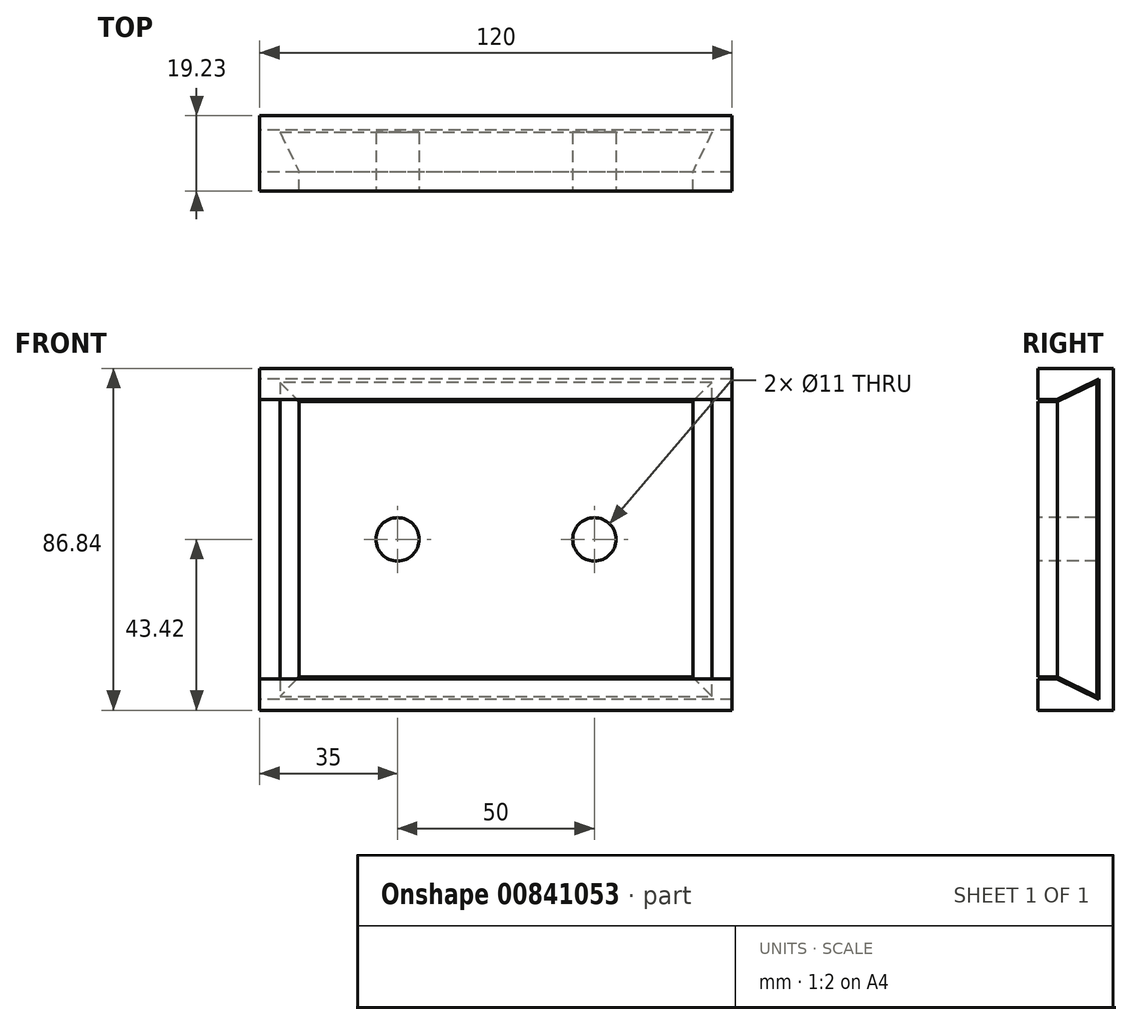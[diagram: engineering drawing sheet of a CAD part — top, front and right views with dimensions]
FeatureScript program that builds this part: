
annotation { "Feature Type Name" : "Feature", "Feature Type Description" : "" }
export const myFeature = defineFeature(function(context is Context, id is Id, definition is map)
    precondition{}
    {
        {
            var Q0;
            Q0=qCreatedBy(makeId("Front.planeOp"),FACE);
            var sketch = newSketch(context, id + "F0", { "sketchPlane" : qUnion([Q0])});
            skLineSegment(sketch, "E0.bottom", {"start": v(-50, -35) * mm, "end": v(50, -35) * mm});
            skLineSegment(sketch, "E0.top", {"start": v(-50, 35) * mm, "end": v(50, 35) * mm});
            skLineSegment(sketch, "E0.left", {"start": v(-50, -35) * mm, "end": v(-50, 35) * mm});
            skLineSegment(sketch, "E0.right", {"start": v(50, -35) * mm, "end": v(50, 35) * mm});
            skSolve(sketch);
        }
        {
            var Q0;
            Q0=makeQuery(id+"F0.imprint","IMPRINT",FACE,{"disambiguationData":[TD([[makeQuery(id+"F0.imprint","IMPRINT",EDGE,{"derivedFrom":sQuery(id+"F0.wireOp",EDGE,"E0.bottom")}),1.0]])]});
            extrude(context, id + "F1", {"entities" : qUnion([Q0]), "oppositeDirection" : true, "depth" : 10 * mm, "offsetDistance" : 25 * mm, "hasDraft" : true, "draftAngle" : 26 * degree});
        }
        {
            var Q0;
            Q0=makeQuery(id+"F1.opExtrude","CAP_FACE",FACE,{"disambiguationData":[OSD([sQuery(id+"F0.wireOp",EDGE,"E0.bottom"),sQuery(id+"F0.wireOp",EDGE,"E0.top"),sQuery(id+"F0.wireOp",EDGE,"E0.left"),sQuery(id+"F0.wireOp",EDGE,"E0.right")])],"isStart":true});
            extrude(context, id + "F2", {"entities" : qUnion([Q0]), "operationType" : NewBodyOperationType.ADD, "depth" : 5 * mm, "offsetDistance" : 25 * mm});
        }
        {
            var Q0;
            Q0=makeQuery(id+"F2.opExtrude","CAP_FACE",FACE,{"disambiguationData":[OSD([sQuery(id+"F0.wireOp",EDGE,"E0.bottom"),sQuery(id+"F0.wireOp",EDGE,"E0.top"),sQuery(id+"F0.wireOp",EDGE,"E0.left"),sQuery(id+"F0.wireOp",EDGE,"E0.right")])],"isStart":false});
            var sketch = newSketch(context, id + "F3", { "sketchPlane" : qUnion([Q0])});
            skPoint(sketch, "E1", {"position": v(-25, 0) * mm});
            skPoint(sketch, "E2", {"position": v(25, 0) * mm});
            skSolve(sketch);
        }
        {
            var Q0;
            Q0=sQuery(id+"F3.wireOp",VERTEX,"E1");
            var Q1;
            Q1=sQuery(id+"F3.wireOp",VERTEX,"E2");
            var Q2;
            Q2=makeQuery(id+"F1.opExtrude","SWEPT_BODY",BODY,{"disambiguationData":[OSD([sQuery(id+"F0.wireOp",EDGE,"E0.bottom"),sQuery(id+"F0.wireOp",EDGE,"E0.top"),sQuery(id+"F0.wireOp",EDGE,"E0.left"),sQuery(id+"F0.wireOp",EDGE,"E0.right")])]});
            hole(context, id + "F4", {"style" : HoleStyle.SIMPLE, "endStyle" : HoleEndStyle.THROUGH, "standardTappedOrClearance" : lookupTablePath({ "fit" : "Normal", "standard" : "ISO", "size" : "M10", "type" : "Clearance" }), "standardBlindInLast" : lookupTablePath({ "fit" : "Standard", "standard" : "ISO", "size" : "M10", "type" : "Clearance" }), "holeDiameter" : 11 * mm, "majorDiameter" : 5 * mm, "isTappedThrough" : true, "tappedDepth" : 12 * mm, "tapClearance" : 3, "locations" : qUnion([Q0, Q1]), "scope" : qUnion([Q2])});
        }
        {
            var Q0;
            Q0=qCreatedBy(makeId("Right.planeOp"),FACE);
            var sketch = newSketch(context, id + "F5", { "sketchPlane" : qUnion([Q0])});
            skLineSegment(sketch, "E3.0", {"start": v(-5, 35.5) * mm, "end": v(-0.12, 35.5) * mm});
            skLineSegment(sketch, "E3.1", {"start": v(-5, -35.5) * mm, "end": v(-0.12, -35.5) * mm});
            skLineSegment(sketch, "E3.2", {"start": v(10.5, -40.68) * mm, "end": v(-0.12, -35.5) * mm});
            skLineSegment(sketch, "E3.3", {"start": v(10.5, -40.68) * mm, "end": v(10.5, 40.68) * mm});
            skLineSegment(sketch, "E3.4", {"start": v(10.5, 40.68) * mm, "end": v(-0.12, 35.5) * mm});
            skLineSegment(sketch, "E4.bottom", {"start": v(-5, 43.42) * mm, "end": v(14.23, 43.42) * mm});
            skLineSegment(sketch, "E4.top", {"start": v(-5, -43.42) * mm, "end": v(14.23, -43.42) * mm});
            skLineSegment(sketch, "E4.left", {"start": v(-5, 43.42) * mm, "end": v(-5, 35.5) * mm});
            skLineSegment(sketch, "E4.right", {"start": v(14.23, 43.42) * mm, "end": v(14.23, -43.42) * mm});
            skLineSegment(sketch, "E5", {"start": v(14.23, 0) * mm, "end": v(-5, 0) * mm, "construction": true});
            skLineSegment(sketch, "E6.trimOffspring", {"start": v(-5, -35.5) * mm, "end": v(-5, -43.42) * mm});
            skSolve(sketch);
        }
        {
            var Q0;
            Q0=makeQuery(id+"F5.imprint","IMPRINT",FACE,{"disambiguationData":[TD([[makeQuery(id+"F5.imprint","IMPRINT",EDGE,{"derivedFrom":sQuery(id+"F5.wireOp",EDGE,"E3.0")}),1.0]])]});
            extrude(context, id + "F6", {"entities" : qUnion([Q0]), "depth" : 60 * mm, "offsetDistance" : 25 * mm, "hasSecondDirection" : true, "secondDirectionOppositeDirection" : true, "secondDirectionDepth" : 60 * mm});
        }
    });
